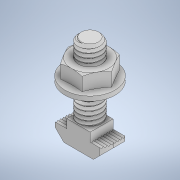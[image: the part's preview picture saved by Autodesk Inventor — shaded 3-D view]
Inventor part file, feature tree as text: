
AUTODESK INVENTOR PART (.ipt)
format: ipt  version: 2020 (Build 240168000, 168)  size: 625,664 bytes
history: native  units: in
note: dims shown in document units (in); Inventor stores cm internally (conversion verified against a paired STEP export)
features: revolve x1, other x1
ambient origin geometry x8: Origin, YZ Plane, XZ Plane, XY Plane, X Axis, Y Axis, Z Axis, Center Point
bodies: Solid1 (feature_tree), Solid2 (feature_tree)
feature tree (2):
  revolve  "Revolve1"  [1 undecoded]
  other  "Cut-Extrude4"
note: 1 required parameter value undecoded (feature->parameter linkage not recoverable at this tier; creation-order binding heuristic only, values carry confidence <= 0.55)
